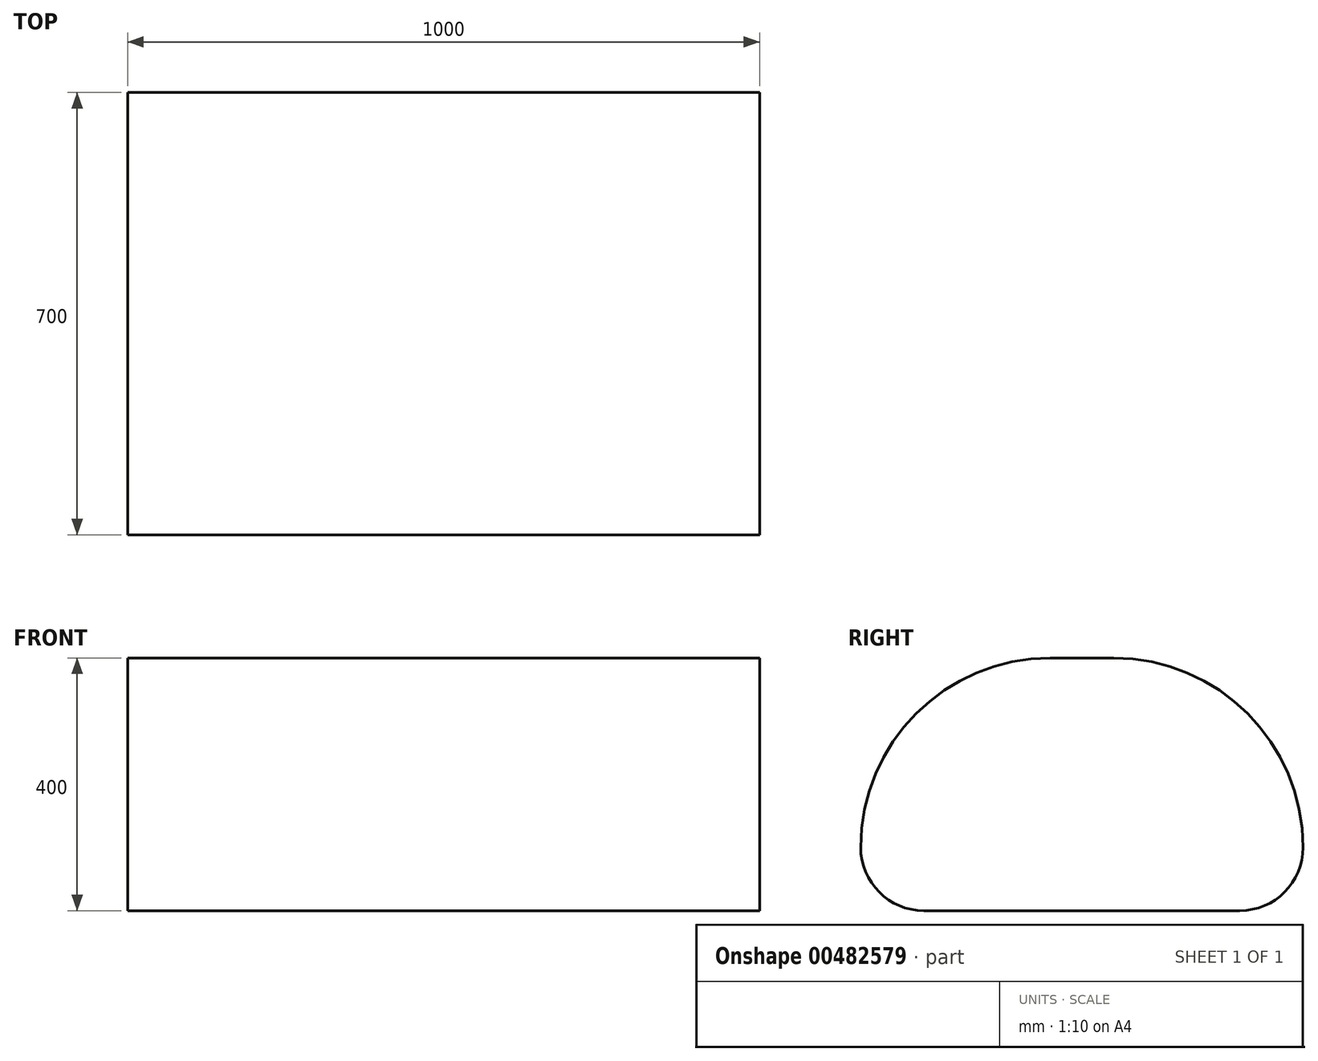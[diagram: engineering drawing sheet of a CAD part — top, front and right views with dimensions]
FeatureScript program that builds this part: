
annotation { "Feature Type Name" : "Feature", "Feature Type Description" : "" }
export const myFeature = defineFeature(function(context is Context, id is Id, definition is map)
    precondition{}
    {
        {
            var Q0;
            Q0=qCreatedBy(makeId("Top.planeOp"),FACE);
            var sketch = newSketch(context, id + "F0", { "sketchPlane" : qUnion([Q0])});
            skLineSegment(sketch, "E0.bottom", {"start": v(500, -350) * mm, "end": v(-500, -350) * mm});
            skLineSegment(sketch, "E0.top", {"start": v(500, 350) * mm, "end": v(-500, 350) * mm});
            skLineSegment(sketch, "E0.left", {"start": v(500, -350) * mm, "end": v(500, 350) * mm});
            skLineSegment(sketch, "E0.right", {"start": v(-500, -350) * mm, "end": v(-500, 350) * mm});
            skPoint(sketch, "E0.middle", {"position": v(0, 0) * mm});
            skSolve(sketch);
        }
        {
            var Q0;
            Q0=makeQuery(id+"F0.imprint","IMPRINT",FACE,{"disambiguationData":[TD([[makeQuery(id+"F0.imprint","IMPRINT",EDGE,{"derivedFrom":sQuery(id+"F0.wireOp",EDGE,"E0.bottom")}),-1.0]])]});
            extrude(context, id + "F1", {"entities" : qUnion([Q0]), "depth" : 400 * mm});
        }
        {
            var Q0;
            Q0=makeQuery(id+"F1.opExtrude","CAP_EDGE",EDGE,{"disambiguationData":[OSD([sQuery(id+"F0.wireOp",EDGE,"E0.bottom")])],"isStart":false});
            var Q1;
            Q1=makeQuery(id+"F1.opExtrude","CAP_EDGE",EDGE,{"disambiguationData":[OSD([sQuery(id+"F0.wireOp",EDGE,"E0.top")])],"isStart":false});
            fillet(context, id + "F2", {"entities" : qUnion([Q0, Q1]), "radius" : 300 * mm, "tangentPropagation" : true, "allowEdgeOverflow" : false});
        }
        {
            var Q0;
            Q0=makeQuery(id+"F1.opExtrude","CAP_EDGE",EDGE,{"disambiguationData":[OSD([sQuery(id+"F0.wireOp",EDGE,"E0.top")])],"isStart":true});
            var Q1;
            Q1=makeQuery(id+"F1.opExtrude","CAP_EDGE",EDGE,{"disambiguationData":[OSD([sQuery(id+"F0.wireOp",EDGE,"E0.bottom")])],"isStart":true});
            fillet(context, id + "F3", {"entities" : qUnion([Q0, Q1]), "radius" : 100 * mm, "tangentPropagation" : true, "allowEdgeOverflow" : false});
        }
    });
